# Revit family: HL Трап для внутренних помещенийHL310NG-SML
name_source: partatom
category: Арматура трубопроводов
units: mm (PartAtom-declared; Revit-internal decimal feet)

## family parameters
Всегда вертикально = Да
Заголовок OmniClass = Deck Waste Water Drains
На основе рабочей плоскости = Нет
Номер OmniClass = 23.70.50.21.24.14
Общий = Да
При загрузке вырезать с полостями = Нет
Размер круглого соединителя = Использовать диаметр
Тип детали = Нормальный

## types (1)
- HL39PrblueG
    CW Connection = Нет
    EAN = 9003076052240
    HW Connection = Нет
    NL_Max = 75 мм
    NL_Min = 20 мм
    URL = https://www.hutterer-lechner.com
    Vent Connection = Нет
    Waste Connection = Да
    ВЕС = 2,179 [kg]
    ВЫСОТА МОНТАЖА = 35-75 mm
    Изготовитель = HL Hutterer & Lechner GmbH
    Ключевая пометка = HL39PrblueG
    Комментарии к типоразмеру = Насадка d 110мм/чугунные подрамники 150х150мм/137х137мм чугун с запахозапирающим устройством Primus.
    МАКСИМАЛЬНАЯ НАГРУЗКА КЛАССА = A/L15 - 1,5 t
    МАТЕРИАЛ = PP, GJL
    Модель = HL39PrblueG
    НАСАДКА = 150x150mm / GJL
    Описание = Трап для внутренних помещений
    Отметка по умолчанию = 0 мм
    РАЗМЕР = d 110 mm
    РЕШЁТКА = 137x137mm / GJL

## geometry (parser evidence)
native form markers: Sweep x83
no freeform markers — native parametric forms only
